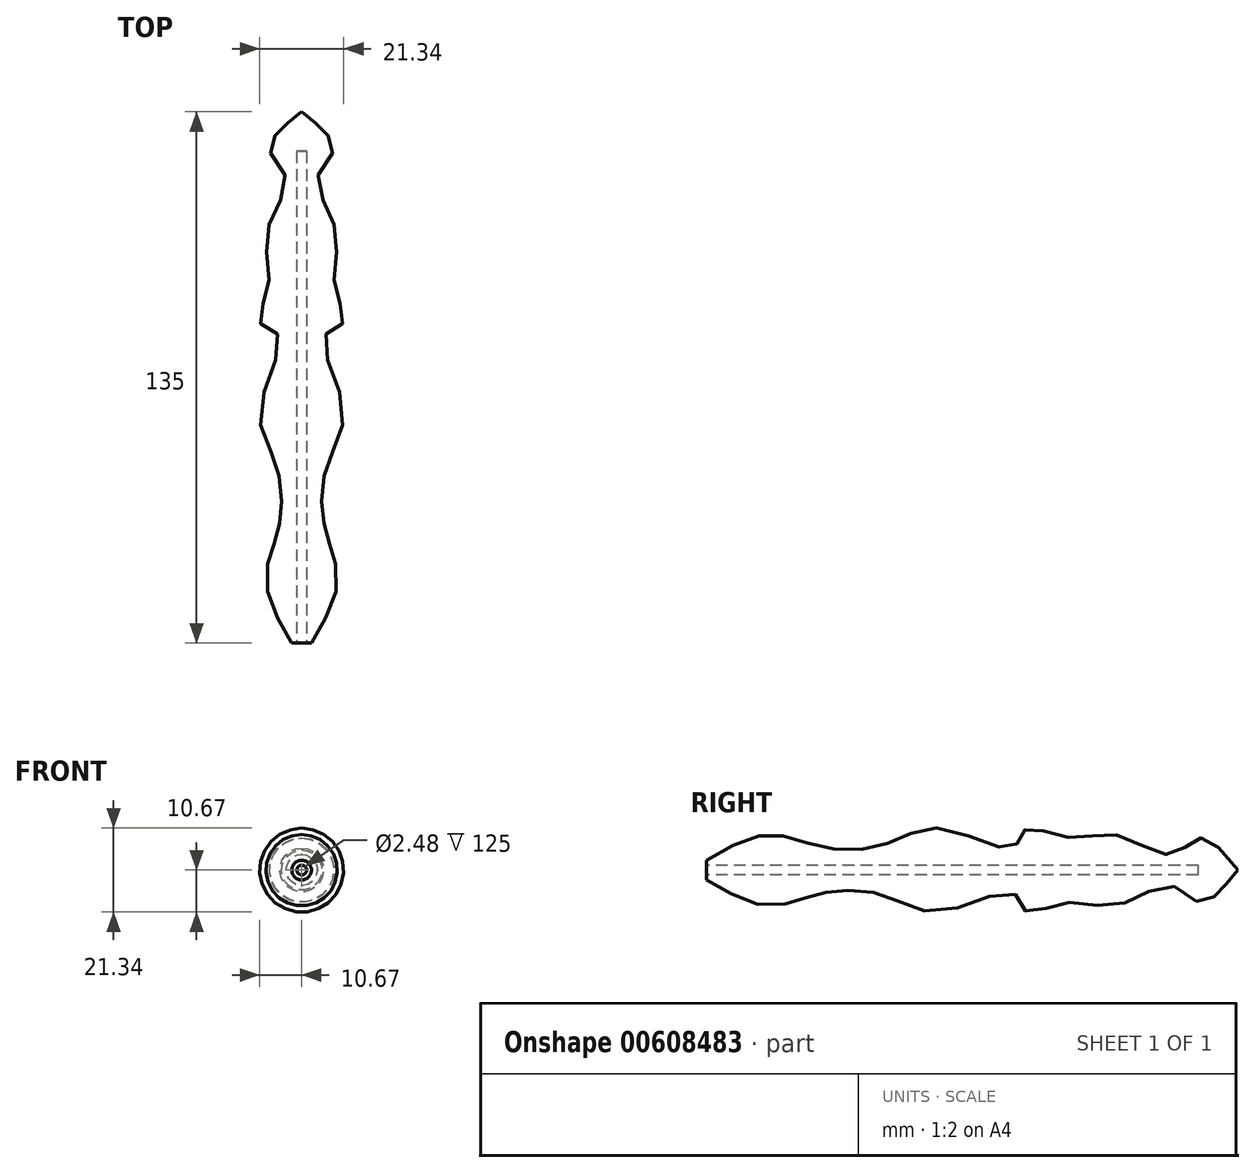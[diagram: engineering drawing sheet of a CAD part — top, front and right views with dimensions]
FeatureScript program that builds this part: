
annotation { "Feature Type Name" : "Feature", "Feature Type Description" : "" }
export const myFeature = defineFeature(function(context is Context, id is Id, definition is map)
    precondition{}
    {
        {
            var Q0;
            Q0=qCreatedBy(makeId("Right.planeOp"),FACE);
            var sketch = newSketch(context, id + "F0", { "sketchPlane" : qUnion([Q0])});
            skLineSegment(sketch, "E0", {"start": v(0, 0) * mm, "end": v(135, 0) * mm});
            skLineSegment(sketch, "E1", {"start": v(0, 0) * mm, "end": v(0, 2.5) * mm});
            skFitSpline(sketch, "E2", {"points": [v(0, 2.5) * mm, v(15.96, 9.06) * mm, v(29.37, 5.85) * mm, v(45.6, 6.6) * mm, v(59.58, 10.57) * mm, v(78.01, 5.8) * mm, v(81.06, 10.35) * mm, v(91.88, 8.3) * mm, v(104.34, 8.87) * mm, v(118.15, 4) * mm, v(125.3, 8.12) * mm, v(135, 0) * mm], "startDerivative": vector(157.69, 92.6) * mm, "endDerivative": vector(118.27, -149.87) * mm});
            skSolve(sketch);
        }
        {
            var Q0;
            Q0=makeQuery(id+"F0.imprint","IMPRINT",FACE,{"disambiguationData":[TD([[makeQuery(id+"F0.imprint","IMPRINT",EDGE,{"derivedFrom":sQuery(id+"F0.wireOp",EDGE,"E0")}),1.0]])]});
            var Q1;
            Q1=sQuery(id+"F0.wireOp",EDGE,"E0");
            revolve(context, id + "F1", {"entities" : qUnion([Q0]), "axis" : qUnion([Q1]), "revolveType" : RevolveType.FULL});
        }
        {
            var Q0;
            Q0=makeQuery(id+"F1.opRevolve","SWEPT_FACE",FACE,{"disambiguationData":[OSD([sQuery(id+"F0.wireOp",EDGE,"E1")])]});
            var sketch = newSketch(context, id + "F2", { "sketchPlane" : qUnion([Q0])});
            skCircle(sketch, "E3", {"center": v(0, 0) * mm, "radius": 1.24 * mm});
            skSolve(sketch);
        }
        {
            var Q0;
            Q0=makeQuery(id+"F2.imprint","IMPRINT",FACE,{"disambiguationData":[TD([[makeQuery(id+"F2.imprint","IMPRINT",EDGE,{"derivedFrom":sQuery(id+"F2.wireOp",EDGE,"E3")}),1.0]])]});
            extrude(context, id + "F3", {"entities" : qUnion([Q0]), "operationType" : NewBodyOperationType.REMOVE, "oppositeDirection" : true, "depth" : 125 * mm, "offsetDistance" : 25 * mm});
        }
    });
